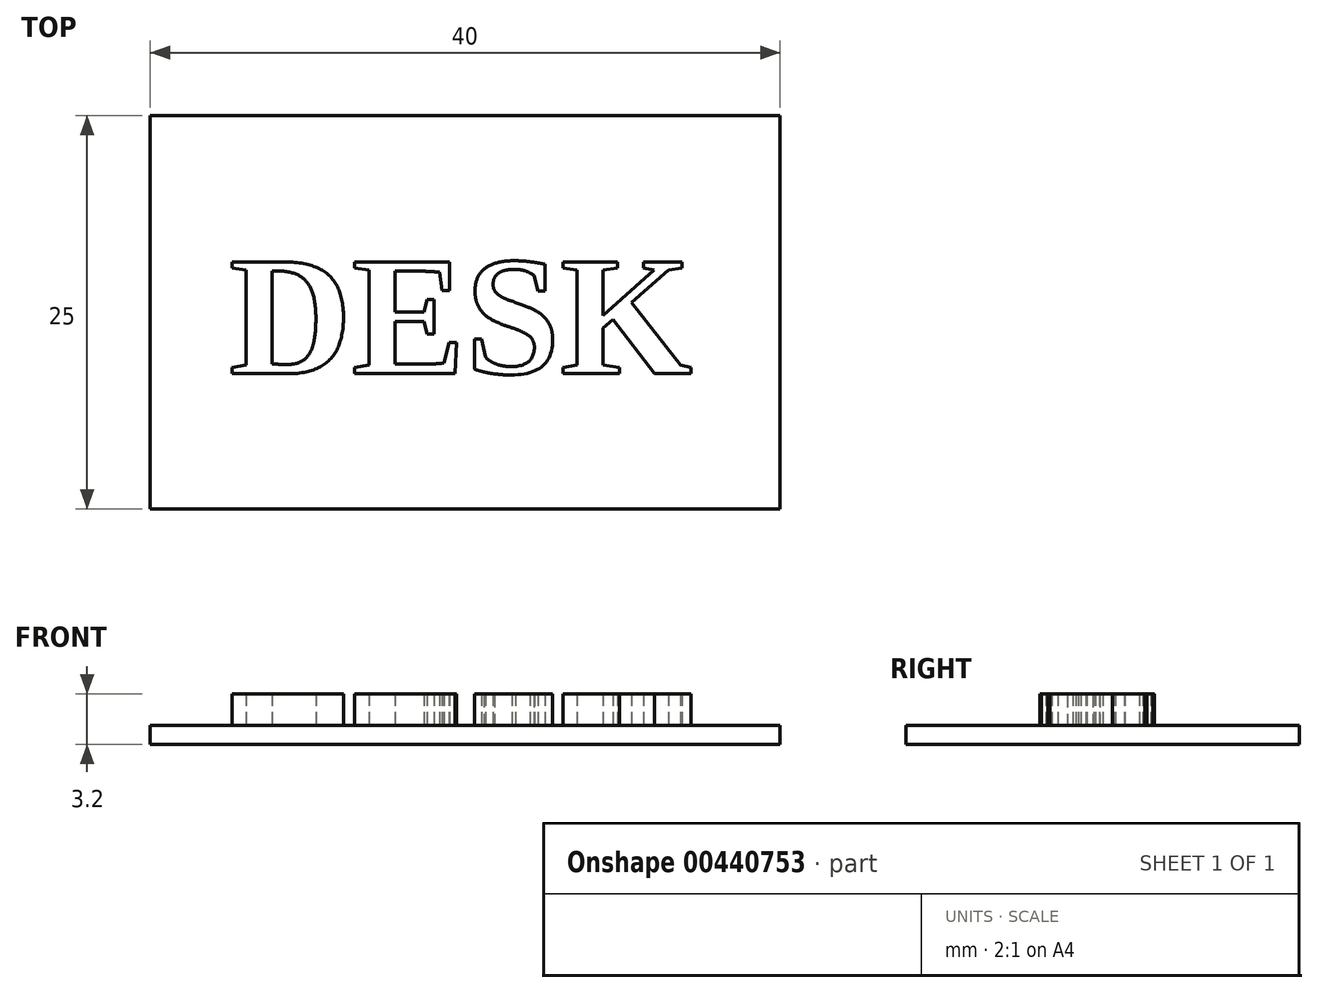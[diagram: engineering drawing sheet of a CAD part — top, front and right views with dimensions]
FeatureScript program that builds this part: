
annotation { "Feature Type Name" : "Feature", "Feature Type Description" : "" }
export const myFeature = defineFeature(function(context is Context, id is Id, definition is map)
    precondition{}
    {
        {
            var Q0;
            Q0=qCreatedBy(makeId("Top.planeOp"),FACE);
            var sketch = newSketch(context, id + "F0", { "sketchPlane" : qUnion([Q0])});
            skLineSegment(sketch, "E0.bottom", {"start": v(0, 0) * mm, "end": v(40, 0) * mm});
            skLineSegment(sketch, "E0.top", {"start": v(0, 25) * mm, "end": v(40, 25) * mm});
            skLineSegment(sketch, "E0.left", {"start": v(0, 0) * mm, "end": v(0, 25) * mm});
            skLineSegment(sketch, "E0.right", {"start": v(40, 0) * mm, "end": v(40, 25) * mm});
            skSolve(sketch);
        }
        {
            var Q0;
            Q0 = qSketchRegion(id + "F0", true);
            extrude(context, id + "F1", {"entities" : qUnion([Q0]), "depth" : 1.2 * mm});
        }
        {
            var Q0;
            Q0=makeQuery(id+"F1.opExtrude","CAP_FACE",FACE,{"disambiguationData":[OSD([sQuery(id+"F0.wireOp",EDGE,"E0.bottom"),sQuery(id+"F0.wireOp",EDGE,"E0.top"),sQuery(id+"F0.wireOp",EDGE,"E0.left"),sQuery(id+"F0.wireOp",EDGE,"E0.right")])],"isStart":false});
            var sketch = newSketch(context, id + "F2", { "sketchPlane" : qUnion([Q0])});
            skText(sketch, "E1", { "text": "DESK", "fontName": "Tinos-Bold.ttf"});
            const initialGuessF2  = {"E1": [0.005, 0.00862, 1, 0, 0.00778]};
            skSetInitialGuess(sketch, initialGuessF2);
            skSolve(sketch);
        }
        {
            var Q0;
            Q0 = qSketchRegion(id + "F2", true);
            extrude(context, id + "F3", {"entities" : qUnion([Q0]), "operationType" : NewBodyOperationType.ADD, "depth" : 2 * mm});
        }
    });
